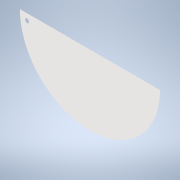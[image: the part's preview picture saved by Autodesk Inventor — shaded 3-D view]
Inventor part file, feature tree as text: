
AUTODESK INVENTOR PART (.ipt)
format: ipt  version: 2021 (Build 250183000, 183)  size: 111,104 bytes
history: native  units: mm
features: other x3, sketch x2, extrude x1, chamfer x1
ambient origin geometry x8: Origin, YZ Plane, XZ Plane, XY Plane, X Axis, Y Axis, Z Axis, Center Point
bodies: Body1 (feature_tree)
feature tree (7):
  other  "Bryła1"
  other  "Powierzchnia1"
  extrude  "Wyciągnięcie proste1"  Depth=1740.0mm
  chamfer  "Faza1"  Distance=3.0mm
  sketch  "Szkic1"
  other  "Płyta1"
  sketch  "Szkic2"
